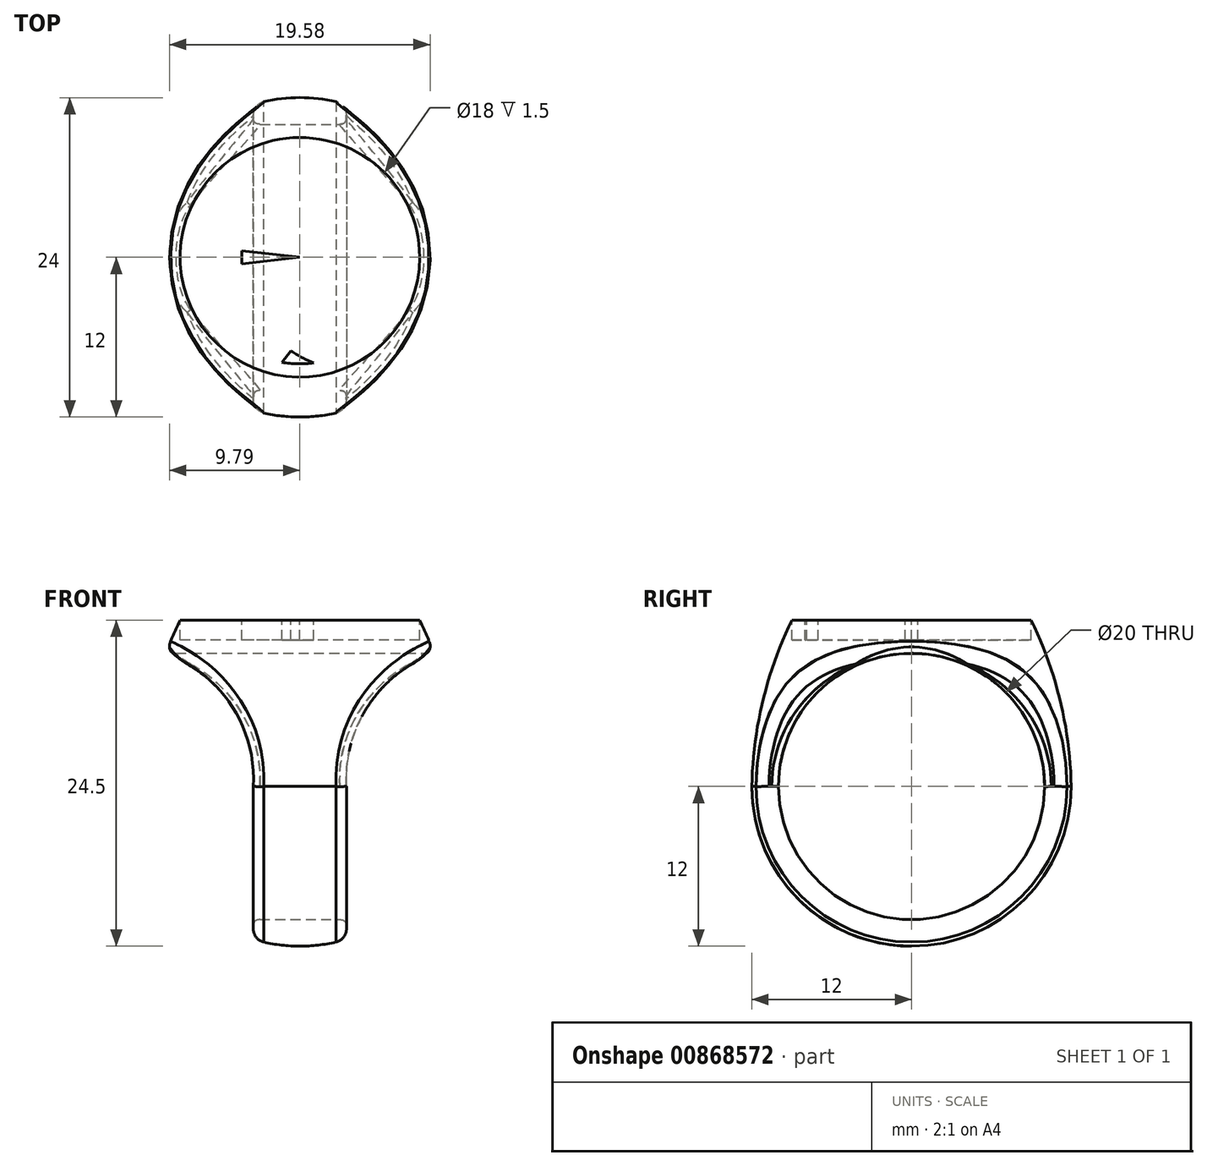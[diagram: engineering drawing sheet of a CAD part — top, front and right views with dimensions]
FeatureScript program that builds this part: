
annotation { "Feature Type Name" : "Feature", "Feature Type Description" : "" }
export const myFeature = defineFeature(function(context is Context, id is Id, definition is map)
    precondition{}
    {
        {
            var Q0;
            Q0=qCreatedBy(makeId("Right.planeOp"),FACE);
            var sketch = newSketch(context, id + "F0", { "sketchPlane" : qUnion([Q0])});
            skLineSegment(sketch, "E0", {"start": v(0, 0) * mm, "end": v(0, -24.5) * mm});
            skLineSegment(sketch, "E1", {"start": v(0, 0) * mm, "end": v(-9, 0) * mm});
            skArc(sketch, "E2", {"start": v(-12, -12.5) * mm, "mid": v(-8.49, -20.99) * mm, "end": v(0, -24.5) * mm});
            skLineSegment(sketch, "E3", {"start": v(0, -12.5) * mm, "end": v(-12, -12.5) * mm, "construction": true});
            skArc(sketch, "E4", {"start": v(-9, 0) * mm, "mid": v(-11.18, -6.09) * mm, "end": v(-12, -12.5) * mm});
            skSolve(sketch);
        }
        {
            var Q0;
            Q0=makeQuery(id+"F0.imprint","IMPRINT",FACE,{"disambiguationData":[TD([[makeQuery(id+"F0.imprint","IMPRINT",EDGE,{"derivedFrom":sQuery(id+"F0.wireOp",EDGE,"E0")}),-1.0]])]});
            var Q1;
            Q1=sQuery(id+"F0.wireOp",EDGE,"E0");
            revolve(context, id + "F1", {"entities" : qUnion([Q0]), "axis" : qUnion([Q1]), "revolveType" : RevolveType.FULL});
        }
        {
            var Q0;
            Q0=qCreatedBy(makeId("Right.planeOp"),FACE);
            var sketch = newSketch(context, id + "F2", { "sketchPlane" : qUnion([Q0])});
            skCircle(sketch, "E5", {"center": v(0, -12.5) * mm, "radius": 10 * mm});
            skSolve(sketch);
        }
        {
            var Q0;
            Q0=qSketchRegion(id+"F2",true);
            extrude(context, id + "F3", {"entities" : qUnion([Q0]), "operationType" : NewBodyOperationType.REMOVE, "endBound" : BoundingType.SYMMETRIC, "oppositeDirection" : true, "depth" : 25 * mm, "offsetDistance" : 25 * mm});
        }
        {
            var Q0;
            Q0=qCreatedBy(makeId("Front.planeOp"),FACE);
            var sketch = newSketch(context, id + "F4", { "sketchPlane" : qUnion([Q0])});
            skLineSegment(sketch, "E6", {"start": v(3.5, -26.5) * mm, "end": v(3.5, -12.5) * mm});
            skArc(sketch, "E7", {"start": v(10.15, -2.5) * mm, "mid": v(5.16, -6.39) * mm, "end": v(3.5, -12.5) * mm});
            skLineSegment(sketch, "E8", {"start": v(10.15, -2.5) * mm, "end": v(11.65, -2.5) * mm});
            skLineSegment(sketch, "E9", {"start": v(11.65, -2.5) * mm, "end": v(11.65, -26.5) * mm});
            skLineSegment(sketch, "E10", {"start": v(11.65, -26.5) * mm, "end": v(3.5, -26.5) * mm});
            skPoint(sketch, "E11.start.orphan", {"position": v(0, -24.5) * mm});
            skLineSegment(sketch, "E12", {"start": v(0, 0) * mm, "end": v(0, -24.5) * mm, "construction": true});
            skLineSegment(sketch, "E13.MirrorCS", {"start": v(-3.5, -26.5) * mm, "end": v(-3.5, -12.5) * mm});
            skArc(sketch, "E14.MirrorCS", {"start": v(-10.15, -2.5) * mm, "mid": v(-5.16, -6.39) * mm, "end": v(-3.5, -12.5) * mm});
            skLineSegment(sketch, "E15.MirrorCS", {"start": v(-11.65, -2.5) * mm, "end": v(-11.65, -26.5) * mm});
            skLineSegment(sketch, "E16.MirrorCS", {"start": v(-11.65, -26.5) * mm, "end": v(-3.5, -26.5) * mm});
            skLineSegment(sketch, "E17.MirrorCS", {"start": v(-10.15, -2.5) * mm, "end": v(-11.65, -2.5) * mm});
            skSolve(sketch);
        }
        {
            var Q0;
            Q0=qSketchRegion(id+"F4",true);
            extrude(context, id + "F5", {"entities" : qUnion([Q0]), "operationType" : NewBodyOperationType.REMOVE, "endBound" : BoundingType.SYMMETRIC, "depth" : 25 * mm, "offsetDistance" : 25 * mm});
        }
        {
            var Q0;
            Q0=makeQuery(id+"F1.opRevolve","SWEPT_FACE",FACE,{"disambiguationData":[OSD([sQuery(id+"F0.wireOp",EDGE,"E1")])]});
            var sketch = newSketch(context, id + "F6", { "sketchPlane" : qUnion([Q0])});
            skLineSegment(sketch, "E18", {"start": v(-8, 0) * mm, "end": v(8, 0) * mm, "construction": true});
            skArc(sketch, "E19", {"start": v(1.04, 7.93) * mm, "mid": v(-0.15, 8) * mm, "end": v(-1.34, 7.89) * mm});
            skLineSegment(sketch, "E20", {"start": v(7.85, 1.55) * mm, "end": v(1.3, 5.96) * mm});
            skLineSegment(sketch, "E21", {"start": v(1.3, 5.96) * mm, "end": v(1.3, 0) * mm});
            skLineSegment(sketch, "E22", {"start": v(8, 0) * mm, "end": v(2.5, 3.7) * mm});
            skLineSegment(sketch, "E23", {"start": v(2.5, 3.7) * mm, "end": v(2.5, 0) * mm});
            skLineSegment(sketch, "E24", {"start": v(0, 0) * mm, "end": v(-7.95, 0.89) * mm});
            skLineSegment(sketch, "E25", {"start": v(0.85, 5.13) * mm, "end": v(-0.14, 6.37) * mm});
            skLineSegment(sketch, "E26", {"start": v(0.85, 5.13) * mm, "end": v(-0.48, 6.13) * mm});
            skLineSegment(sketch, "E27", {"start": v(0.4, 3.12) * mm, "end": v(-1.85, 4.8) * mm});
            skLineSegment(sketch, "E28", {"start": v(0.4, 3.12) * mm, "end": v(-2.2, 4.3) * mm});
            skLineSegment(sketch, "E29", {"start": v(0, 1.63) * mm, "end": v(-2.97, 2.88) * mm});
            skLineSegment(sketch, "E30", {"start": v(0, 1.63) * mm, "end": v(-3.24, 2.09) * mm});
            skArc(sketch, "E31", {"start": v(2.7, 7.53) * mm, "mid": v(1.22, 7.1) * mm, "end": v(-0.14, 6.37) * mm});
            skArc(sketch, "E32", {"start": v(1.04, 7.93) * mm, "mid": v(0.16, 7.53) * mm, "end": v(-0.66, 7.03) * mm});
            skLineSegment(sketch, "E33.MirrorCS", {"start": v(8, 0) * mm, "end": v(2.5, -3.7) * mm});
            skLineSegment(sketch, "E34.MirrorCS", {"start": v(7.85, -1.55) * mm, "end": v(1.3, -5.96) * mm});
            skLineSegment(sketch, "E35.MirrorCS", {"start": v(2.5, -3.7) * mm, "end": v(2.5, 0) * mm});
            skLineSegment(sketch, "E36.MirrorCS", {"start": v(1.3, -5.96) * mm, "end": v(1.3, 0) * mm});
            skLineSegment(sketch, "E37.MirrorCS", {"start": v(0, 0) * mm, "end": v(-7.95, -0.89) * mm});
            skArc(sketch, "E38.MirrorCS", {"start": v(2.7, -7.53) * mm, "mid": v(1.22, -7.1) * mm, "end": v(-0.14, -6.37) * mm});
            skArc(sketch, "E39.MirrorCS", {"start": v(1.04, -7.93) * mm, "mid": v(0.16, -7.53) * mm, "end": v(-0.66, -7.03) * mm});
            skLineSegment(sketch, "E40.MirrorCS", {"start": v(0, -1.63) * mm, "end": v(-3.24, -2.09) * mm});
            skLineSegment(sketch, "E41.MirrorCS", {"start": v(0, -1.63) * mm, "end": v(-2.97, -2.88) * mm});
            skLineSegment(sketch, "E42.MirrorCS", {"start": v(0.4, -3.12) * mm, "end": v(-2.2, -4.3) * mm});
            skLineSegment(sketch, "E43.MirrorCS", {"start": v(0.4, -3.12) * mm, "end": v(-1.85, -4.8) * mm});
            skLineSegment(sketch, "E44.MirrorCS", {"start": v(0.85, -5.13) * mm, "end": v(-0.48, -6.13) * mm});
            skLineSegment(sketch, "E45.MirrorCS", {"start": v(0.85, -5.13) * mm, "end": v(-0.14, -6.37) * mm});
            skArc(sketch, "E46.trimOffspring", {"start": v(-1.17, 6.65) * mm, "mid": v(-1.89, 6.02) * mm, "end": v(-2.53, 5.3) * mm});
            skLineSegment(sketch, "E47.trimOffspring", {"start": v(-0.66, 7.03) * mm, "end": v(-1.34, 7.89) * mm});
            skLineSegment(sketch, "E48.trimOffspring", {"start": v(-1.17, 6.65) * mm, "end": v(-2.45, 7.62) * mm});
            skArc(sketch, "E49.trimOffspring", {"start": v(-0.48, 6.13) * mm, "mid": v(-1.2, 5.5) * mm, "end": v(-1.85, 4.8) * mm});
            skArc(sketch, "E50.trimOffspring", {"start": v(7.85, 1.55) * mm, "mid": v(6.06, 5.22) * mm, "end": v(2.7, 7.53) * mm});
            skLineSegment(sketch, "E51.trimOffspring", {"start": v(-2.53, 5.3) * mm, "end": v(-4.39, 6.7) * mm});
            skArc(sketch, "E52.trimOffspring", {"start": v(-2.99, 4.66) * mm, "mid": v(-3.4, 3.95) * mm, "end": v(-3.75, 3.21) * mm});
            skArc(sketch, "E53.trimOffspring", {"start": v(-2.2, 4.3) * mm, "mid": v(-2.63, 3.61) * mm, "end": v(-2.97, 2.88) * mm});
            skLineSegment(sketch, "E54.trimOffspring", {"start": v(-2.99, 4.66) * mm, "end": v(-5.5, 5.8) * mm});
            skArc(sketch, "E55.trimOffspring", {"start": v(-2.45, 7.62) * mm, "mid": v(-3.45, 7.22) * mm, "end": v(-4.39, 6.7) * mm});
            skArc(sketch, "E56.trimOffspring", {"start": v(-5.5, 5.8) * mm, "mid": v(-6.12, 5.16) * mm, "end": v(-6.66, 4.44) * mm});
            skArc(sketch, "E57.trimOffspring", {"start": v(-3.24, 2.09) * mm, "mid": v(-3.46, 1.05) * mm, "end": v(-3.53, 0) * mm});
            skLineSegment(sketch, "E58.trimOffspring", {"start": v(-3.75, 3.21) * mm, "end": v(-6.66, 4.44) * mm});
            skArc(sketch, "E59.trimOffspring", {"start": v(-4.08, 2.2) * mm, "mid": v(-4.3, 1.11) * mm, "end": v(-4.38, 0) * mm});
            skLineSegment(sketch, "E60.trimOffspring", {"start": v(-4.08, 2.2) * mm, "end": v(-7.53, 2.7) * mm});
            skArc(sketch, "E61.trimOffspring", {"start": v(-7.53, 2.7) * mm, "mid": v(-7.8, 1.8) * mm, "end": v(-7.95, 0.89) * mm});
            skArc(sketch, "E62.trimOffspring", {"start": v(-7.95, -0.89) * mm, "mid": v(-7.8, -1.8) * mm, "end": v(-7.53, -2.7) * mm});
            skArc(sketch, "E63.trimOffspring", {"start": v(-6.66, -4.44) * mm, "mid": v(-6.12, -5.16) * mm, "end": v(-5.5, -5.8) * mm});
            skArc(sketch, "E64.trimOffspring", {"start": v(-4.39, -6.7) * mm, "mid": v(-3.45, -7.22) * mm, "end": v(-2.45, -7.62) * mm});
            skArc(sketch, "E65.trimOffspring", {"start": v(-1.34, -7.89) * mm, "mid": v(-0.15, -8) * mm, "end": v(1.04, -7.93) * mm});
            skArc(sketch, "E66.trimOffspring", {"start": v(2.7, -7.53) * mm, "mid": v(6.06, -5.22) * mm, "end": v(7.85, -1.55) * mm});
            skLineSegment(sketch, "E67.trimOffspring", {"start": v(-0.66, -7.03) * mm, "end": v(-1.34, -7.89) * mm});
            skArc(sketch, "E68.trimOffspring", {"start": v(-1.17, -6.65) * mm, "mid": v(-1.89, -6.02) * mm, "end": v(-2.53, -5.3) * mm});
            skLineSegment(sketch, "E69.trimOffspring", {"start": v(-1.17, -6.65) * mm, "end": v(-2.45, -7.62) * mm});
            skArc(sketch, "E70.trimOffspring", {"start": v(-0.48, -6.13) * mm, "mid": v(-1.2, -5.5) * mm, "end": v(-1.85, -4.8) * mm});
            skLineSegment(sketch, "E71.trimOffspring", {"start": v(-2.53, -5.3) * mm, "end": v(-4.39, -6.7) * mm});
            skArc(sketch, "E72.trimOffspring", {"start": v(-2.2, -4.3) * mm, "mid": v(-2.63, -3.61) * mm, "end": v(-2.97, -2.88) * mm});
            skLineSegment(sketch, "E73.trimOffspring", {"start": v(-2.99, -4.66) * mm, "end": v(-5.5, -5.8) * mm});
            skArc(sketch, "E74.trimOffspring", {"start": v(-2.99, -4.66) * mm, "mid": v(-3.4, -3.95) * mm, "end": v(-3.75, -3.21) * mm});
            skLineSegment(sketch, "E75.trimOffspring", {"start": v(-3.75, -3.21) * mm, "end": v(-6.66, -4.44) * mm});
            skArc(sketch, "E76.trimOffspring", {"start": v(-3.24, -2.09) * mm, "mid": v(-3.46, -1.05) * mm, "end": v(-3.53, 0) * mm});
            skLineSegment(sketch, "E77.trimOffspring", {"start": v(-4.08, -2.2) * mm, "end": v(-7.53, -2.7) * mm});
            skArc(sketch, "E78.trimOffspring", {"start": v(-4.08, -2.2) * mm, "mid": v(-4.3, -1.11) * mm, "end": v(-4.38, 0) * mm});
            skSolve(sketch);
        }
        {
            var Q0;
            {var subQ4=sQuery(id+"F6.wireOp",EDGE,"E60.trimOffspring");Q0=makeQuery(id+"F6.imprint","IMPRINT",FACE,{"disambiguationData":[TD([[makeQuery(id+"F6.imprint","IMPRINT",EDGE,{"derivedFrom":subQ4}),1.0]])]});}
            var Q1;
            Q1=makeQuery(id+"F6.imprint","IMPRINT",FACE,{"disambiguationData":[TD([[makeQuery(id+"F6.imprint","IMPRINT",EDGE,{"derivedFrom":sQuery(id+"F6.wireOp",EDGE,"E52.trimOffspring")}),-1.0]])]});
            var Q2;
            Q2=makeQuery(id+"F6.imprint","IMPRINT",FACE,{"disambiguationData":[TD([[makeQuery(id+"F6.imprint","IMPRINT",EDGE,{"derivedFrom":sQuery(id+"F6.wireOp",EDGE,"E46.trimOffspring")}),-1.0]])]});
            var Q3;
            Q3=makeQuery(id+"F6.imprint","IMPRINT",FACE,{"disambiguationData":[TD([[makeQuery(id+"F6.imprint","IMPRINT",EDGE,{"derivedFrom":sQuery(id+"F6.wireOp",EDGE,"E19")}),1.0]])]});
            var Q4;
            Q4=makeQuery(id+"F6.imprint","IMPRINT",FACE,{"disambiguationData":[TD([[makeQuery(id+"F6.imprint","IMPRINT",EDGE,{"derivedFrom":sQuery(id+"F6.wireOp",EDGE,"E20")}),-1.0]])]});
            var Q5;
            Q5=makeQuery(id+"F6.imprint","IMPRINT",FACE,{"disambiguationData":[TD([[makeQuery(id+"F6.imprint","IMPRINT",EDGE,{"derivedFrom":sQuery(id+"F6.wireOp",EDGE,"E22")}),1.0]])]});
            var Q6;
            {var subQ0=sQuery(id+"F6.wireOp",EDGE,"E62.trimOffspring");Q6=makeQuery(id+"F6.imprint","IMPRINT",FACE,{"disambiguationData":[TD([[makeQuery(id+"F6.imprint","IMPRINT",EDGE,{"derivedFrom":subQ0}),1.0]])]});}
            var Q7;
            Q7=makeQuery(id+"F6.imprint","IMPRINT",FACE,{"disambiguationData":[TD([[makeQuery(id+"F6.imprint","IMPRINT",EDGE,{"derivedFrom":sQuery(id+"F6.wireOp",EDGE,"E63.trimOffspring")}),1.0]])]});
            var Q8;
            Q8=makeQuery(id+"F6.imprint","IMPRINT",FACE,{"disambiguationData":[TD([[makeQuery(id+"F6.imprint","IMPRINT",EDGE,{"derivedFrom":sQuery(id+"F6.wireOp",EDGE,"E64.trimOffspring")}),1.0]])]});
            var Q9;
            Q9=makeQuery(id+"F6.imprint","IMPRINT",FACE,{"disambiguationData":[TD([[makeQuery(id+"F6.imprint","IMPRINT",EDGE,{"derivedFrom":sQuery(id+"F6.wireOp",EDGE,"E39.MirrorCS")}),1.0]])]});
            extrude(context, id + "F7", {"entities" : qUnion([Q0, Q1, Q2, Q3, Q4, Q5, Q6, Q7, Q8, Q9]), "operationType" : NewBodyOperationType.REMOVE, "oppositeDirection" : true, "depth" : 1.5 * mm, "offsetDistance" : 25 * mm});
        }
        {
            var Q0;
            Q0=makeQuery(id+"F5.boolean.opBoolean","INTERSECT",EDGE,{"disambiguationData":[OD(1.0)],"derivedFrom":[makeQuery(id+"F1.opRevolve","SWEPT_FACE",FACE,{"disambiguationData":[OSD([sQuery(id+"F0.wireOp",EDGE,"E4")])]}),makeQuery(id+"F5.opExtrude","SWEPT_FACE",FACE,{"disambiguationData":[OSD([sQuery(id+"F4.wireOp",EDGE,"E14.MirrorCS")])]})]});
            var Q1;
            Q1=makeQuery(id+"F5.boolean.opBoolean","INTERSECT",EDGE,{"derivedFrom":[makeQuery(id+"F1.opRevolve","SWEPT_FACE",FACE,{"disambiguationData":[OSD([sQuery(id+"F0.wireOp",EDGE,"E2")])]}),makeQuery(id+"F5.opExtrude","SWEPT_FACE",FACE,{"disambiguationData":[OSD([sQuery(id+"F4.wireOp",EDGE,"E13.MirrorCS")])]})]});
            var Q2;
            Q2=makeQuery(id+"F5.boolean.opBoolean","INTERSECT",EDGE,{"disambiguationData":[OD(1.0)],"derivedFrom":[makeQuery(id+"F1.opRevolve","SWEPT_FACE",FACE,{"disambiguationData":[OSD([sQuery(id+"F0.wireOp",EDGE,"E4")])]}),makeQuery(id+"F5.opExtrude","SWEPT_FACE",FACE,{"disambiguationData":[OSD([sQuery(id+"F4.wireOp",EDGE,"E7")])]})]});
            var Q3;
            Q3=makeQuery(id+"F5.boolean.opBoolean","INTERSECT",EDGE,{"derivedFrom":[makeQuery(id+"F1.opRevolve","SWEPT_FACE",FACE,{"disambiguationData":[OSD([sQuery(id+"F0.wireOp",EDGE,"E2")])]}),makeQuery(id+"F5.opExtrude","SWEPT_FACE",FACE,{"disambiguationData":[OSD([sQuery(id+"F4.wireOp",EDGE,"E6")])]})]});
            fillet(context, id + "F8", {"entities" : qUnion([Q0, Q1, Q2, Q3]), "radius" : 1 * mm, "allowEdgeOverflow" : false});
        }
        {
            var Q0;
            Q0=makeQuery(id+"F5.boolean.opBoolean","INTERSECT",EDGE,{"disambiguationData":[OD(1.0)],"derivedFrom":[makeQuery(id+"F3.boolean.opBoolean","COPY",FACE,{"derivedFrom":makeQuery(id+"F3.opExtrude","SWEPT_FACE",FACE,{"disambiguationData":[OSD([sQuery(id+"F2.wireOp",EDGE,"E5")])]})}),makeQuery(id+"F5.opExtrude","SWEPT_FACE",FACE,{"disambiguationData":[OSD([sQuery(id+"F4.wireOp",EDGE,"E14.MirrorCS")])]})]});
            var Q1;
            Q1=makeQuery(id+"F5.boolean.opBoolean","INTERSECT",EDGE,{"derivedFrom":[makeQuery(id+"F3.boolean.opBoolean","COPY",FACE,{"derivedFrom":makeQuery(id+"F3.opExtrude","SWEPT_FACE",FACE,{"disambiguationData":[OSD([sQuery(id+"F2.wireOp",EDGE,"E5")])]})}),makeQuery(id+"F5.opExtrude","SWEPT_FACE",FACE,{"disambiguationData":[OSD([sQuery(id+"F4.wireOp",EDGE,"E13.MirrorCS")])]})]});
            var Q2;
            Q2=makeQuery(id+"F5.boolean.opBoolean","INTERSECT",EDGE,{"disambiguationData":[OD(0.0)],"derivedFrom":[makeQuery(id+"F3.boolean.opBoolean","COPY",FACE,{"derivedFrom":makeQuery(id+"F3.opExtrude","SWEPT_FACE",FACE,{"disambiguationData":[OSD([sQuery(id+"F2.wireOp",EDGE,"E5")])]})}),makeQuery(id+"F5.opExtrude","SWEPT_FACE",FACE,{"disambiguationData":[OSD([sQuery(id+"F4.wireOp",EDGE,"E14.MirrorCS")])]})]});
            var Q3;
            Q3=makeQuery(id+"F5.boolean.opBoolean","INTERSECT",EDGE,{"disambiguationData":[OD(0.0)],"derivedFrom":[makeQuery(id+"F3.boolean.opBoolean","COPY",FACE,{"derivedFrom":makeQuery(id+"F3.opExtrude","SWEPT_FACE",FACE,{"disambiguationData":[OSD([sQuery(id+"F2.wireOp",EDGE,"E5")])]})}),makeQuery(id+"F5.opExtrude","SWEPT_FACE",FACE,{"disambiguationData":[OSD([sQuery(id+"F4.wireOp",EDGE,"E7")])]})]});
            var Q4;
            Q4=makeQuery(id+"F3.boolean.opBoolean","COPY",FACE,{"derivedFrom":makeQuery(id+"F3.opExtrude","SWEPT_FACE",FACE,{"disambiguationData":[OSD([sQuery(id+"F2.wireOp",EDGE,"E5")])]})});
            fillet(context, id + "F9", {"entities" : qUnion([Q0, Q1, Q2, Q3, Q4]), "radius" : .5 * mm, "rho" : 0.5, "crossSection" : FilletCrossSection.CONIC, "allowEdgeOverflow" : false});
        }
    });
